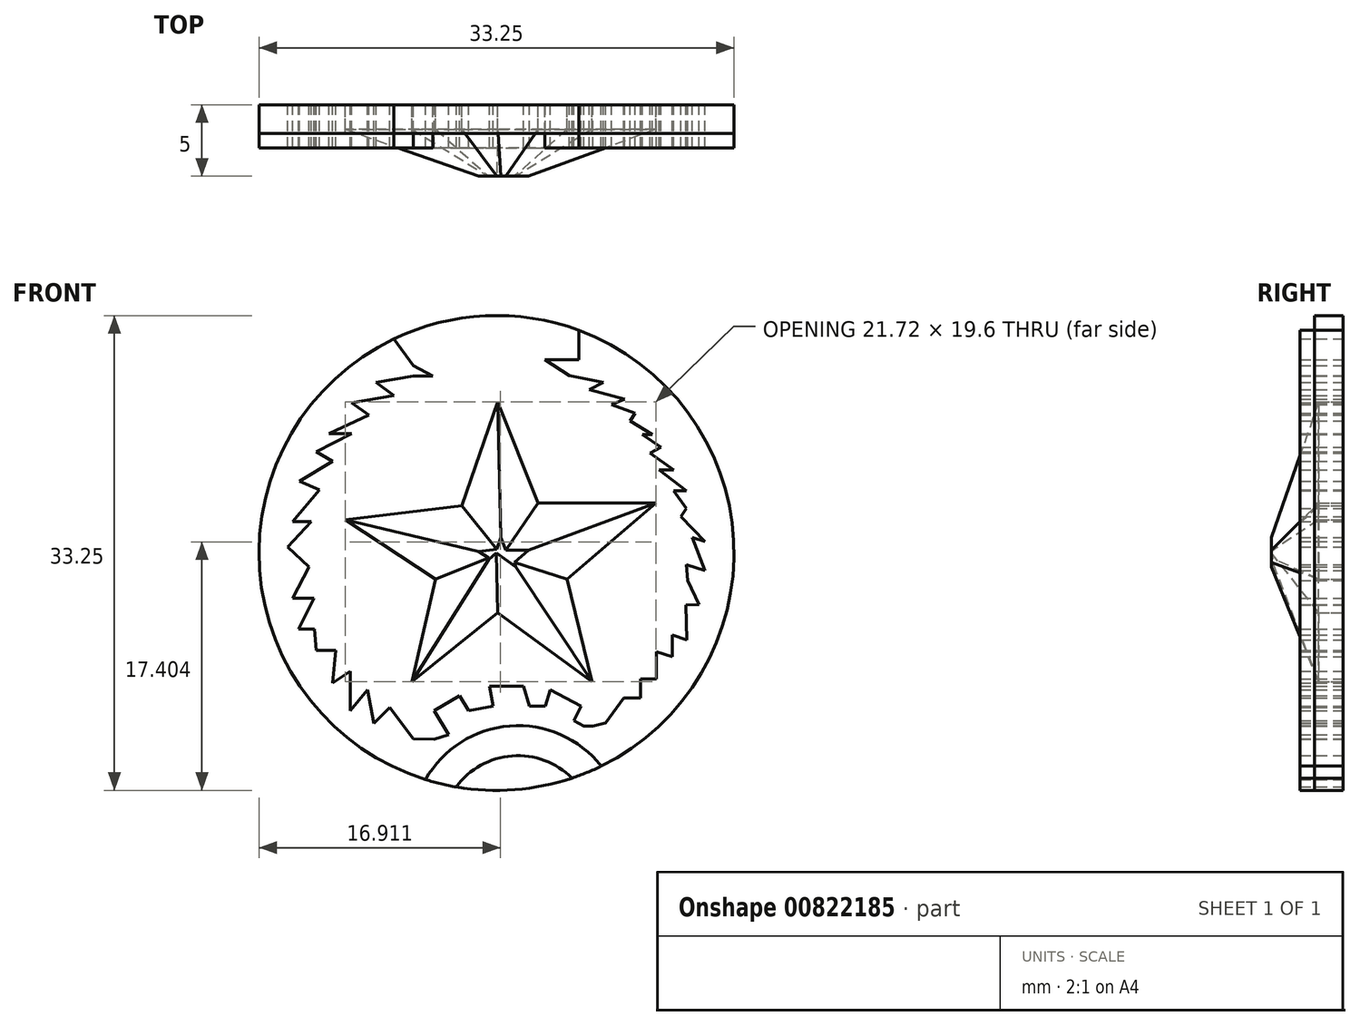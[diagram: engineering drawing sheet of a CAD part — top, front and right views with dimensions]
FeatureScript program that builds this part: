
annotation { "Feature Type Name" : "Feature", "Feature Type Description" : "" }
export const myFeature = defineFeature(function(context is Context, id is Id, definition is map)
    precondition{}
    {
        {
            var Q0;
            Q0=qCreatedBy(makeId("Front.planeOp"),FACE);
            var sketch = newSketch(context, id + "F0", { "sketchPlane" : qUnion([Q0])});
            skLineSegment(sketch, "E0", {"start": v(-2.81, 15.91) * mm, "end": v(-5.33, 8.63) * mm});
            skLineSegment(sketch, "E1", {"start": v(-5.33, 8.63) * mm, "end": v(-13.48, 7.66) * mm});
            skLineSegment(sketch, "E2", {"start": v(-13.48, 7.66) * mm, "end": v(-7.18, 3.5) * mm});
            skLineSegment(sketch, "E3", {"start": v(-7.18, 3.5) * mm, "end": v(-8.83, -3.69) * mm});
            skPoint(sketch, "E4.end.orphan", {"position": v(-2.81, 0) * mm});
            skLineSegment(sketch, "E5", {"start": v(-8.83, -3.69) * mm, "end": v(-2.81, 1.16) * mm});
            skLineSegment(sketch, "E6", {"start": v(-2.81, 1.16) * mm, "end": v(3.78, -3.69) * mm});
            skLineSegment(sketch, "E7", {"start": v(3.78, -3.69) * mm, "end": v(2.04, 3.5) * mm});
            skLineSegment(sketch, "E8", {"start": v(2.04, 3.5) * mm, "end": v(8.24, 8.83) * mm});
            skLineSegment(sketch, "E9", {"start": v(8.24, 8.83) * mm, "end": v(0, 8.83) * mm});
            skLineSegment(sketch, "E10", {"start": v(0, 8.83) * mm, "end": v(-2.81, 15.91) * mm});
            skCircle(sketch, "E11", {"center": v(-2.9, 5.33) * mm, "radius": 16.62 * mm});
            skLineSegment(sketch, "E12", {"start": v(-8.73, -7.66) * mm, "end": v(-7.26, -7.7) * mm});
            skLineSegment(sketch, "E13", {"start": v(-6.25, -7.39) * mm, "end": v(-7.26, -5.72) * mm});
            skLineSegment(sketch, "E14", {"start": v(-7.26, -5.72) * mm, "end": v(-5.5, -4.65) * mm});
            skLineSegment(sketch, "E15", {"start": v(-5.5, -4.65) * mm, "end": v(-4.84, -5.72) * mm});
            skLineSegment(sketch, "E16", {"start": v(-4.84, -5.72) * mm, "end": v(-3.13, -5.4) * mm});
            skLineSegment(sketch, "E17", {"start": v(-3.13, -5.4) * mm, "end": v(-3.4, -4) * mm});
            skLineSegment(sketch, "E18", {"start": v(-3.4, -4) * mm, "end": v(-1.01, -4) * mm});
            skLineSegment(sketch, "E19", {"start": v(-1.01, -4) * mm, "end": v(-0.6, -5.4) * mm});
            skLineSegment(sketch, "E20", {"start": v(-0.6, -5.4) * mm, "end": v(0.5, -5.4) * mm});
            skLineSegment(sketch, "E21", {"start": v(0.5, -5.4) * mm, "end": v(0.86, -4.25) * mm});
            skLineSegment(sketch, "E22", {"start": v(0.86, -4.25) * mm, "end": v(3.02, -5.4) * mm});
            skLineSegment(sketch, "E23", {"start": v(3.02, -5.4) * mm, "end": v(2.5, -6.4) * mm});
            skLineSegment(sketch, "E24", {"start": v(2.5, -6.4) * mm, "end": v(3.21, -6.78) * mm});
            skLineSegment(sketch, "E25", {"start": v(3.21, -6.78) * mm, "end": v(3.84, -6.78) * mm});
            skLineSegment(sketch, "E26", {"start": v(-7.26, -7.7) * mm, "end": v(-6.25, -7.39) * mm});
            skLineSegment(sketch, "E27", {"start": v(4.74, -6.58) * mm, "end": v(6, -4.82) * mm});
            skPoint(sketch, "E27.endSnap0", {"position": v(0.68, -4.82) * mm});
            skLineSegment(sketch, "E28", {"start": v(6, -4.82) * mm, "end": v(7.18, -4.82) * mm});
            skLineSegment(sketch, "E29", {"start": v(7.18, -4.82) * mm, "end": v(7.18, -3.48) * mm});
            skLineSegment(sketch, "E30", {"start": v(7.18, -3.48) * mm, "end": v(8.28, -3.48) * mm});
            skLineSegment(sketch, "E31", {"start": v(8.28, -3.48) * mm, "end": v(8.28, -1.58) * mm});
            skLineSegment(sketch, "E32", {"start": v(8.28, -1.58) * mm, "end": v(9.4, -1.93) * mm});
            skLineSegment(sketch, "E33", {"start": v(9.4, -1.93) * mm, "end": v(9.4, -0.42) * mm});
            skLineSegment(sketch, "E34", {"start": v(9.4, -0.42) * mm, "end": v(10.42, -0.75) * mm});
            skLineSegment(sketch, "E35", {"start": v(10.42, -0.75) * mm, "end": v(10.35, 1.7) * mm});
            skLineSegment(sketch, "E36", {"start": v(10.35, 1.7) * mm, "end": v(11.27, 1.73) * mm});
            skLineSegment(sketch, "E37", {"start": v(11.27, 1.73) * mm, "end": v(10.48, 3.41) * mm});
            skLineSegment(sketch, "E38", {"start": v(10.48, 3.41) * mm, "end": v(10.38, 4.53) * mm});
            skLineSegment(sketch, "E39", {"start": v(10.38, 4.53) * mm, "end": v(11.7, 4.1) * mm});
            skLineSegment(sketch, "E40", {"start": v(11.7, 4.1) * mm, "end": v(10.79, 6.43) * mm});
            skLineSegment(sketch, "E41", {"start": v(10.79, 6.43) * mm, "end": v(11.67, 6.15) * mm});
            skLineSegment(sketch, "E42", {"start": v(11.67, 6.15) * mm, "end": v(10, 7.88) * mm});
            skLineSegment(sketch, "E43", {"start": v(10, 7.88) * mm, "end": v(10.38, 8.47) * mm});
            skLineSegment(sketch, "E44", {"start": v(10.38, 8.47) * mm, "end": v(9.5, 9.68) * mm});
            skLineSegment(sketch, "E45", {"start": v(9.5, 9.68) * mm, "end": v(10.38, 9.68) * mm});
            skLineSegment(sketch, "E46", {"start": v(10.38, 9.68) * mm, "end": v(8.49, 11.16) * mm});
            skLineSegment(sketch, "E47", {"start": v(8.49, 11.16) * mm, "end": v(9.5, 11.16) * mm});
            skLineSegment(sketch, "E48", {"start": v(9.5, 11.16) * mm, "end": v(7.83, 12.34) * mm});
            skLineSegment(sketch, "E49", {"start": v(7.83, 12.34) * mm, "end": v(8.6, 12.75) * mm});
            skLineSegment(sketch, "E50", {"start": v(8.6, 12.75) * mm, "end": v(7.3, 13.63) * mm});
            skLineSegment(sketch, "E51", {"start": v(7.3, 13.63) * mm, "end": v(8, 13.63) * mm});
            skLineSegment(sketch, "E52", {"start": v(8, 13.63) * mm, "end": v(6.44, 14.58) * mm});
            skLineSegment(sketch, "E53", {"start": v(6.44, 14.58) * mm, "end": v(6.8, 15.12) * mm});
            skLineSegment(sketch, "E54", {"start": v(6.8, 15.12) * mm, "end": v(5.16, 15.72) * mm});
            skLineSegment(sketch, "E55", {"start": v(5.16, 15.72) * mm, "end": v(6.07, 16.11) * mm});
            skLineSegment(sketch, "E56", {"start": v(6.07, 16.11) * mm, "end": v(3.6, 16.77) * mm});
            skLineSegment(sketch, "E57", {"start": v(3.6, 16.77) * mm, "end": v(4.57, 17.28) * mm});
            skLineSegment(sketch, "E58", {"start": v(4.57, 17.28) * mm, "end": v(2.19, 17.74) * mm});
            skLineSegment(sketch, "E59", {"start": v(2.19, 17.74) * mm, "end": v(0.48, 18.88) * mm});
            skLineSegment(sketch, "E60", {"start": v(0.48, 18.88) * mm, "end": v(2.85, 18.88) * mm});
            skLineSegment(sketch, "E61", {"start": v(3.84, -6.78) * mm, "end": v(4.74, -6.58) * mm});
            skLineSegment(sketch, "E62", {"start": v(2.85, 18.88) * mm, "end": v(2.85, 20.93) * mm});
            skLineSegment(sketch, "E63", {"start": v(-8.73, -7.66) * mm, "end": v(-10.4, -5.48) * mm});
            skLineSegment(sketch, "E64", {"start": v(-10.4, -5.48) * mm, "end": v(-11.49, -6.58) * mm});
            skLineSegment(sketch, "E65", {"start": v(-11.49, -6.58) * mm, "end": v(-11.93, -4.24) * mm});
            skLineSegment(sketch, "E66", {"start": v(-11.93, -4.24) * mm, "end": v(-13.13, -5.7) * mm});
            skLineSegment(sketch, "E67", {"start": v(-13.13, -5.7) * mm, "end": v(-13.13, -2.94) * mm});
            skLineSegment(sketch, "E68", {"start": v(-13.13, -2.94) * mm, "end": v(-14.37, -3.77) * mm});
            skLineSegment(sketch, "E69", {"start": v(-14.37, -3.77) * mm, "end": v(-14.15, -1.5) * mm});
            skLineSegment(sketch, "E70", {"start": v(-14.15, -1.5) * mm, "end": v(-15.53, -1.5) * mm});
            skLineSegment(sketch, "E71", {"start": v(-15.53, -1.5) * mm, "end": v(-15.66, 0) * mm});
            skLineSegment(sketch, "E72", {"start": v(-15.66, 0) * mm, "end": v(-16.77, 0) * mm});
            skLineSegment(sketch, "E73", {"start": v(-16.77, 0) * mm, "end": v(-15.67, 2.16) * mm});
            skLineSegment(sketch, "E74", {"start": v(-15.67, 2.16) * mm, "end": v(-17.18, 2.16) * mm});
            skLineSegment(sketch, "E75", {"start": v(-17.18, 2.16) * mm, "end": v(-16.03, 4.37) * mm});
            skLineSegment(sketch, "E76", {"start": v(-16.03, 4.37) * mm, "end": v(-17.52, 5.76) * mm});
            skLineSegment(sketch, "E77", {"start": v(-17.52, 5.76) * mm, "end": v(-15.88, 7.53) * mm});
            skLineSegment(sketch, "E78", {"start": v(-15.88, 7.53) * mm, "end": v(-17.18, 7.53) * mm});
            skLineSegment(sketch, "E79", {"start": v(-17.18, 7.53) * mm, "end": v(-15.3, 9.75) * mm});
            skLineSegment(sketch, "E80", {"start": v(-15.3, 9.75) * mm, "end": v(-16.7, 10.35) * mm});
            skLineSegment(sketch, "E81", {"start": v(-16.7, 10.35) * mm, "end": v(-14.38, 11.77) * mm});
            skLineSegment(sketch, "E82", {"start": v(-14.38, 11.77) * mm, "end": v(-15.53, 12.41) * mm});
            skLineSegment(sketch, "E83", {"start": v(-15.53, 12.41) * mm, "end": v(-13.05, 13.7) * mm});
            skLineSegment(sketch, "E84", {"start": v(-13.05, 13.7) * mm, "end": v(-14.64, 13.7) * mm});
            skLineSegment(sketch, "E85", {"start": v(-14.64, 13.7) * mm, "end": v(-11.83, 15) * mm});
            skLineSegment(sketch, "E86", {"start": v(-11.83, 15) * mm, "end": v(-13.07, 15.84) * mm});
            skLineSegment(sketch, "E87", {"start": v(-13.07, 15.84) * mm, "end": v(-10.08, 16.36) * mm});
            skLineSegment(sketch, "E88", {"start": v(-10.08, 16.36) * mm, "end": v(-11.35, 17.28) * mm});
            skLineSegment(sketch, "E89", {"start": v(-11.35, 17.28) * mm, "end": v(-8.73, 17.71) * mm});
            skLineSegment(sketch, "E90", {"start": v(-8.73, 17.71) * mm, "end": v(-7.36, 17.71) * mm});
            skLineSegment(sketch, "E91", {"start": v(-7.36, 17.71) * mm, "end": v(-8.73, 18.45) * mm});
            skLineSegment(sketch, "E92", {"start": v(-8.73, 18.45) * mm, "end": v(-10.08, 20.33) * mm});
            skArc(sketch, "E93", {"start": v(4.43, -9.58) * mm, "mid": v(-1.98, -6.78) * mm, "end": v(-7.88, -10.53) * mm});
            skArc(sketch, "E94.0", {"start": v(2.37, -10.43) * mm, "mid": v(-1.82, -8.87) * mm, "end": v(-5.72, -11.05) * mm});
            skLineSegment(sketch, "E95", {"start": v(-7.18, 3.5) * mm, "end": v(-2.9, 5.33) * mm});
            skLineSegment(sketch, "E96", {"start": v(-13.48, 7.66) * mm, "end": v(-2.9, 5.33) * mm});
            skLineSegment(sketch, "E97", {"start": v(-5.33, 8.63) * mm, "end": v(-2.9, 5.33) * mm});
            skLineSegment(sketch, "E98", {"start": v(0, 8.83) * mm, "end": v(-2.9, 5.33) * mm});
            skLineSegment(sketch, "E99", {"start": v(2.04, 3.5) * mm, "end": v(-2.9, 5.33) * mm});
            skLineSegment(sketch, "E100", {"start": v(8.24, 8.83) * mm, "end": v(-2.9, 5.33) * mm});
            skLineSegment(sketch, "E101", {"start": v(-8.83, -3.69) * mm, "end": v(-2.9, 5.33) * mm});
            skLineSegment(sketch, "E102", {"start": v(-2.81, 1.16) * mm, "end": v(-2.9, 5.33) * mm});
            skLineSegment(sketch, "E103", {"start": v(3.78, -3.69) * mm, "end": v(-2.9, 5.33) * mm});
            skLineSegment(sketch, "E104", {"start": v(-2.81, 15.91) * mm, "end": v(-2.9, 5.33) * mm});
            skSolve(sketch);
        }
        {
            var Q0;
            Q0=makeQuery(id+"F0.imprint","IMPRINT",FACE,{"disambiguationData":[TD([[makeQuery(id+"F0.imprint","IMPRINT",EDGE,{"derivedFrom":sQuery(id+"F0.wireOp",EDGE,"E0")}),1.0]])]});
            var Q1;
            Q1=makeQuery(id+"F0.imprint","IMPRINT",FACE,{"disambiguationData":[TD([[makeQuery(id+"F0.imprint","IMPRINT",EDGE,{"derivedFrom":sQuery(id+"F0.wireOp",EDGE,"E12")}),-1.0]])]});
            var Q2;
            {var subQ0=sQuery(id+"F0.wireOp",EDGE,"E94.0");Q2=makeQuery(id+"F0.imprint","IMPRINT",FACE,{"disambiguationData":[TD([[makeQuery(id+"F0.imprint","IMPRINT",EDGE,{"derivedFrom":subQ0}),1.0]])]});}
            var Q3;
            Q3=makeQuery(id+"F0.imprint","IMPRINT",FACE,{"disambiguationData":[TD([[makeQuery(id+"F0.imprint","IMPRINT",EDGE,{"derivedFrom":sQuery(id+"F0.wireOp",EDGE,"E10")}),1.0]])]});
            var Q4;
            Q4=makeQuery(id+"F0.imprint","IMPRINT",FACE,{"disambiguationData":[TD([[makeQuery(id+"F0.imprint","IMPRINT",EDGE,{"derivedFrom":sQuery(id+"F0.wireOp",EDGE,"E1")}),1.0]])]});
            var Q5;
            Q5=makeQuery(id+"F0.imprint","IMPRINT",FACE,{"disambiguationData":[TD([[makeQuery(id+"F0.imprint","IMPRINT",EDGE,{"derivedFrom":sQuery(id+"F0.wireOp",EDGE,"E2")}),1.0]])]});
            var Q6;
            Q6=makeQuery(id+"F0.imprint","IMPRINT",FACE,{"disambiguationData":[TD([[makeQuery(id+"F0.imprint","IMPRINT",EDGE,{"derivedFrom":sQuery(id+"F0.wireOp",EDGE,"E9")}),1.0]])]});
            var Q7;
            Q7=makeQuery(id+"F0.imprint","IMPRINT",FACE,{"disambiguationData":[TD([[makeQuery(id+"F0.imprint","IMPRINT",EDGE,{"derivedFrom":sQuery(id+"F0.wireOp",EDGE,"E8")}),1.0]])]});
            var Q8;
            Q8=makeQuery(id+"F0.imprint","IMPRINT",FACE,{"disambiguationData":[TD([[makeQuery(id+"F0.imprint","IMPRINT",EDGE,{"derivedFrom":sQuery(id+"F0.wireOp",EDGE,"E3")}),1.0]])]});
            var Q9;
            Q9=makeQuery(id+"F0.imprint","IMPRINT",FACE,{"disambiguationData":[TD([[makeQuery(id+"F0.imprint","IMPRINT",EDGE,{"derivedFrom":sQuery(id+"F0.wireOp",EDGE,"E5")}),1.0]])]});
            var Q10;
            Q10=makeQuery(id+"F0.imprint","IMPRINT",FACE,{"disambiguationData":[TD([[makeQuery(id+"F0.imprint","IMPRINT",EDGE,{"derivedFrom":sQuery(id+"F0.wireOp",EDGE,"E6")}),1.0]])]});
            var Q11;
            Q11=makeQuery(id+"F0.imprint","IMPRINT",FACE,{"disambiguationData":[TD([[makeQuery(id+"F0.imprint","IMPRINT",EDGE,{"derivedFrom":sQuery(id+"F0.wireOp",EDGE,"E7")}),1.0]])]});
            extrude(context, id + "F1", {"entities" : qUnion([Q0, Q1, Q2, Q3, Q4, Q5, Q6, Q7, Q8, Q9, Q10, Q11]), "depth" : 3 * mm, "offsetDistance" : 25 * mm});
        }
        {
            var Q0;
            Q0 = qSketchRegion(id + "F0", true);
            extrude(context, id + "F2", {"entities" : qUnion([Q0]), "depth" : 2 * mm, "offsetDistance" : 25 * mm});
        }
        {
            var Q0;
            Q0=makeQuery(id+"F1.opExtrude","CAP_FACE",FACE,{"disambiguationData":[OSD([sQuery(id+"F0.wireOp",EDGE,"E0"),sQuery(id+"F0.wireOp",EDGE,"E1"),sQuery(id+"F0.wireOp",EDGE,"E2"),sQuery(id+"F0.wireOp",EDGE,"E3"),sQuery(id+"F0.wireOp",EDGE,"E5"),sQuery(id+"F0.wireOp",EDGE,"E6"),sQuery(id+"F0.wireOp",EDGE,"E7"),sQuery(id+"F0.wireOp",EDGE,"E8"),sQuery(id+"F0.wireOp",EDGE,"E9"),sQuery(id+"F0.wireOp",EDGE,"E10")])],"isStart":false});
            extrude(context, id + "F3", {"entities" : qUnion([Q0]), "operationType" : NewBodyOperationType.ADD, "depth" : 2 * mm, "offsetDistance" : 25 * mm});
        }
        {
            var Q0;
            Q0=makeQuery(id+"F3.opExtrude","CAP_FACE",FACE,{"disambiguationData":[OSD([sQuery(id+"F0.wireOp",EDGE,"E0"),sQuery(id+"F0.wireOp",EDGE,"E1"),sQuery(id+"F0.wireOp",EDGE,"E2"),sQuery(id+"F0.wireOp",EDGE,"E3"),sQuery(id+"F0.wireOp",EDGE,"E5"),sQuery(id+"F0.wireOp",EDGE,"E6"),sQuery(id+"F0.wireOp",EDGE,"E7"),sQuery(id+"F0.wireOp",EDGE,"E8"),sQuery(id+"F0.wireOp",EDGE,"E9"),sQuery(id+"F0.wireOp",EDGE,"E10")])],"isStart":false});
            chamfer(context, id + "F4", {"entities" : qUnion([Q0]), "width" : 3.3 * mm, "tangentPropagation" : true});
        }
        {
            var Q0;
            Q0=makeQuery(id+"F1.opExtrude","CAP_FACE",FACE,{"disambiguationData":[OSD([sQuery(id+"F0.wireOp",EDGE,"E11"),sQuery(id+"F0.wireOp",EDGE,"E12"),sQuery(id+"F0.wireOp",EDGE,"E13"),sQuery(id+"F0.wireOp",EDGE,"E14"),sQuery(id+"F0.wireOp",EDGE,"E15"),sQuery(id+"F0.wireOp",EDGE,"E16"),sQuery(id+"F0.wireOp",EDGE,"E17"),sQuery(id+"F0.wireOp",EDGE,"E18"),sQuery(id+"F0.wireOp",EDGE,"E19"),sQuery(id+"F0.wireOp",EDGE,"E20"),sQuery(id+"F0.wireOp",EDGE,"E21"),sQuery(id+"F0.wireOp",EDGE,"E22"),sQuery(id+"F0.wireOp",EDGE,"E23"),sQuery(id+"F0.wireOp",EDGE,"E24"),sQuery(id+"F0.wireOp",EDGE,"E25"),sQuery(id+"F0.wireOp",EDGE,"E26"),sQuery(id+"F0.wireOp",EDGE,"E27"),sQuery(id+"F0.wireOp",EDGE,"E28"),sQuery(id+"F0.wireOp",EDGE,"E29"),sQuery(id+"F0.wireOp",EDGE,"E30"),sQuery(id+"F0.wireOp",EDGE,"E31"),sQuery(id+"F0.wireOp",EDGE,"E32"),sQuery(id+"F0.wireOp",EDGE,"E33"),sQuery(id+"F0.wireOp",EDGE,"E34"),sQuery(id+"F0.wireOp",EDGE,"E35"),sQuery(id+"F0.wireOp",EDGE,"E36"),sQuery(id+"F0.wireOp",EDGE,"E37"),sQuery(id+"F0.wireOp",EDGE,"E38"),sQuery(id+"F0.wireOp",EDGE,"E39"),sQuery(id+"F0.wireOp",EDGE,"E40"),sQuery(id+"F0.wireOp",EDGE,"E41"),sQuery(id+"F0.wireOp",EDGE,"E42"),sQuery(id+"F0.wireOp",EDGE,"E43"),sQuery(id+"F0.wireOp",EDGE,"E44"),sQuery(id+"F0.wireOp",EDGE,"E45"),sQuery(id+"F0.wireOp",EDGE,"E46"),sQuery(id+"F0.wireOp",EDGE,"E47"),sQuery(id+"F0.wireOp",EDGE,"E48"),sQuery(id+"F0.wireOp",EDGE,"E49"),sQuery(id+"F0.wireOp",EDGE,"E50"),sQuery(id+"F0.wireOp",EDGE,"E51"),sQuery(id+"F0.wireOp",EDGE,"E52"),sQuery(id+"F0.wireOp",EDGE,"E53"),sQuery(id+"F0.wireOp",EDGE,"E54"),sQuery(id+"F0.wireOp",EDGE,"E55"),sQuery(id+"F0.wireOp",EDGE,"E56"),sQuery(id+"F0.wireOp",EDGE,"E57"),sQuery(id+"F0.wireOp",EDGE,"E58"),sQuery(id+"F0.wireOp",EDGE,"E59"),sQuery(id+"F0.wireOp",EDGE,"E60"),sQuery(id+"F0.wireOp",EDGE,"E61"),sQuery(id+"F0.wireOp",EDGE,"E62"),sQuery(id+"F0.wireOp",EDGE,"E63"),sQuery(id+"F0.wireOp",EDGE,"E64"),sQuery(id+"F0.wireOp",EDGE,"E65"),sQuery(id+"F0.wireOp",EDGE,"E66"),sQuery(id+"F0.wireOp",EDGE,"E67"),sQuery(id+"F0.wireOp",EDGE,"E68"),sQuery(id+"F0.wireOp",EDGE,"E69"),sQuery(id+"F0.wireOp",EDGE,"E70"),sQuery(id+"F0.wireOp",EDGE,"E71"),sQuery(id+"F0.wireOp",EDGE,"E72"),sQuery(id+"F0.wireOp",EDGE,"E73"),sQuery(id+"F0.wireOp",EDGE,"E74"),sQuery(id+"F0.wireOp",EDGE,"E75"),sQuery(id+"F0.wireOp",EDGE,"E76"),sQuery(id+"F0.wireOp",EDGE,"E77"),sQuery(id+"F0.wireOp",EDGE,"E78"),sQuery(id+"F0.wireOp",EDGE,"E79"),sQuery(id+"F0.wireOp",EDGE,"E80"),sQuery(id+"F0.wireOp",EDGE,"E81"),sQuery(id+"F0.wireOp",EDGE,"E82"),sQuery(id+"F0.wireOp",EDGE,"E83"),sQuery(id+"F0.wireOp",EDGE,"E84"),sQuery(id+"F0.wireOp",EDGE,"E85"),sQuery(id+"F0.wireOp",EDGE,"E86"),sQuery(id+"F0.wireOp",EDGE,"E87"),sQuery(id+"F0.wireOp",EDGE,"E88"),sQuery(id+"F0.wireOp",EDGE,"E89"),sQuery(id+"F0.wireOp",EDGE,"E90"),sQuery(id+"F0.wireOp",EDGE,"E91"),sQuery(id+"F0.wireOp",EDGE,"E92"),sQuery(id+"F0.wireOp",EDGE,"E93")])],"isStart":false});
            extrude(context, id + "F5", {"entities" : qUnion([Q0]), "operationType" : NewBodyOperationType.ADD, "depth" : 2 * mm, "offsetDistance" : 25 * mm});
        }
        {
            var Q0;
            Q0=makeQuery(id+"F1.opExtrude","CAP_FACE",FACE,{"disambiguationData":[OSD([sQuery(id+"F0.wireOp",EDGE,"E11"),sQuery(id+"F0.wireOp",EDGE,"E94.0")])],"isStart":false});
            extrude(context, id + "F6", {"entities" : qUnion([Q0]), "operationType" : NewBodyOperationType.ADD, "depth" : 2 * mm, "offsetDistance" : 25 * mm});
        }
        {
            var Q0;
            Q0=makeQuery(id+"F5.opExtrude","CAP_FACE",FACE,{"disambiguationData":[OSD([sQuery(id+"F0.wireOp",EDGE,"E11"),sQuery(id+"F0.wireOp",EDGE,"E12"),sQuery(id+"F0.wireOp",EDGE,"E13"),sQuery(id+"F0.wireOp",EDGE,"E14"),sQuery(id+"F0.wireOp",EDGE,"E15"),sQuery(id+"F0.wireOp",EDGE,"E16"),sQuery(id+"F0.wireOp",EDGE,"E17"),sQuery(id+"F0.wireOp",EDGE,"E18"),sQuery(id+"F0.wireOp",EDGE,"E19"),sQuery(id+"F0.wireOp",EDGE,"E20"),sQuery(id+"F0.wireOp",EDGE,"E21"),sQuery(id+"F0.wireOp",EDGE,"E22"),sQuery(id+"F0.wireOp",EDGE,"E23"),sQuery(id+"F0.wireOp",EDGE,"E24"),sQuery(id+"F0.wireOp",EDGE,"E25"),sQuery(id+"F0.wireOp",EDGE,"E26"),sQuery(id+"F0.wireOp",EDGE,"E27"),sQuery(id+"F0.wireOp",EDGE,"E28"),sQuery(id+"F0.wireOp",EDGE,"E29"),sQuery(id+"F0.wireOp",EDGE,"E30"),sQuery(id+"F0.wireOp",EDGE,"E31"),sQuery(id+"F0.wireOp",EDGE,"E32"),sQuery(id+"F0.wireOp",EDGE,"E33"),sQuery(id+"F0.wireOp",EDGE,"E34"),sQuery(id+"F0.wireOp",EDGE,"E35"),sQuery(id+"F0.wireOp",EDGE,"E36"),sQuery(id+"F0.wireOp",EDGE,"E37"),sQuery(id+"F0.wireOp",EDGE,"E38"),sQuery(id+"F0.wireOp",EDGE,"E39"),sQuery(id+"F0.wireOp",EDGE,"E40"),sQuery(id+"F0.wireOp",EDGE,"E41"),sQuery(id+"F0.wireOp",EDGE,"E42"),sQuery(id+"F0.wireOp",EDGE,"E43"),sQuery(id+"F0.wireOp",EDGE,"E44"),sQuery(id+"F0.wireOp",EDGE,"E45"),sQuery(id+"F0.wireOp",EDGE,"E46"),sQuery(id+"F0.wireOp",EDGE,"E47"),sQuery(id+"F0.wireOp",EDGE,"E48"),sQuery(id+"F0.wireOp",EDGE,"E49"),sQuery(id+"F0.wireOp",EDGE,"E50"),sQuery(id+"F0.wireOp",EDGE,"E51"),sQuery(id+"F0.wireOp",EDGE,"E52"),sQuery(id+"F0.wireOp",EDGE,"E53"),sQuery(id+"F0.wireOp",EDGE,"E54"),sQuery(id+"F0.wireOp",EDGE,"E55"),sQuery(id+"F0.wireOp",EDGE,"E56"),sQuery(id+"F0.wireOp",EDGE,"E57"),sQuery(id+"F0.wireOp",EDGE,"E58"),sQuery(id+"F0.wireOp",EDGE,"E59"),sQuery(id+"F0.wireOp",EDGE,"E60"),sQuery(id+"F0.wireOp",EDGE,"E61"),sQuery(id+"F0.wireOp",EDGE,"E62"),sQuery(id+"F0.wireOp",EDGE,"E63"),sQuery(id+"F0.wireOp",EDGE,"E64"),sQuery(id+"F0.wireOp",EDGE,"E65"),sQuery(id+"F0.wireOp",EDGE,"E66"),sQuery(id+"F0.wireOp",EDGE,"E67"),sQuery(id+"F0.wireOp",EDGE,"E68"),sQuery(id+"F0.wireOp",EDGE,"E69"),sQuery(id+"F0.wireOp",EDGE,"E70"),sQuery(id+"F0.wireOp",EDGE,"E71"),sQuery(id+"F0.wireOp",EDGE,"E72"),sQuery(id+"F0.wireOp",EDGE,"E73"),sQuery(id+"F0.wireOp",EDGE,"E74"),sQuery(id+"F0.wireOp",EDGE,"E75"),sQuery(id+"F0.wireOp",EDGE,"E76"),sQuery(id+"F0.wireOp",EDGE,"E77"),sQuery(id+"F0.wireOp",EDGE,"E78"),sQuery(id+"F0.wireOp",EDGE,"E79"),sQuery(id+"F0.wireOp",EDGE,"E80"),sQuery(id+"F0.wireOp",EDGE,"E81"),sQuery(id+"F0.wireOp",EDGE,"E82"),sQuery(id+"F0.wireOp",EDGE,"E83"),sQuery(id+"F0.wireOp",EDGE,"E84"),sQuery(id+"F0.wireOp",EDGE,"E85"),sQuery(id+"F0.wireOp",EDGE,"E86"),sQuery(id+"F0.wireOp",EDGE,"E87"),sQuery(id+"F0.wireOp",EDGE,"E88"),sQuery(id+"F0.wireOp",EDGE,"E89"),sQuery(id+"F0.wireOp",EDGE,"E90"),sQuery(id+"F0.wireOp",EDGE,"E91"),sQuery(id+"F0.wireOp",EDGE,"E92"),sQuery(id+"F0.wireOp",EDGE,"E93")])],"isStart":false});
            extrude(context, id + "F7", {"entities" : qUnion([Q0]), "operationType" : NewBodyOperationType.REMOVE, "depth" : 2 * mm, "offsetDistance" : 25 * mm});
        }
        {
            var Q0;
            Q0=makeQuery(id+"F5.opExtrude","CAP_FACE",FACE,{"disambiguationData":[OSD([sQuery(id+"F0.wireOp",EDGE,"E11"),sQuery(id+"F0.wireOp",EDGE,"E12"),sQuery(id+"F0.wireOp",EDGE,"E13"),sQuery(id+"F0.wireOp",EDGE,"E14"),sQuery(id+"F0.wireOp",EDGE,"E15"),sQuery(id+"F0.wireOp",EDGE,"E16"),sQuery(id+"F0.wireOp",EDGE,"E17"),sQuery(id+"F0.wireOp",EDGE,"E18"),sQuery(id+"F0.wireOp",EDGE,"E19"),sQuery(id+"F0.wireOp",EDGE,"E20"),sQuery(id+"F0.wireOp",EDGE,"E21"),sQuery(id+"F0.wireOp",EDGE,"E22"),sQuery(id+"F0.wireOp",EDGE,"E23"),sQuery(id+"F0.wireOp",EDGE,"E24"),sQuery(id+"F0.wireOp",EDGE,"E25"),sQuery(id+"F0.wireOp",EDGE,"E26"),sQuery(id+"F0.wireOp",EDGE,"E27"),sQuery(id+"F0.wireOp",EDGE,"E28"),sQuery(id+"F0.wireOp",EDGE,"E29"),sQuery(id+"F0.wireOp",EDGE,"E30"),sQuery(id+"F0.wireOp",EDGE,"E31"),sQuery(id+"F0.wireOp",EDGE,"E32"),sQuery(id+"F0.wireOp",EDGE,"E33"),sQuery(id+"F0.wireOp",EDGE,"E34"),sQuery(id+"F0.wireOp",EDGE,"E35"),sQuery(id+"F0.wireOp",EDGE,"E36"),sQuery(id+"F0.wireOp",EDGE,"E37"),sQuery(id+"F0.wireOp",EDGE,"E38"),sQuery(id+"F0.wireOp",EDGE,"E39"),sQuery(id+"F0.wireOp",EDGE,"E40"),sQuery(id+"F0.wireOp",EDGE,"E41"),sQuery(id+"F0.wireOp",EDGE,"E42"),sQuery(id+"F0.wireOp",EDGE,"E43"),sQuery(id+"F0.wireOp",EDGE,"E44"),sQuery(id+"F0.wireOp",EDGE,"E45"),sQuery(id+"F0.wireOp",EDGE,"E46"),sQuery(id+"F0.wireOp",EDGE,"E47"),sQuery(id+"F0.wireOp",EDGE,"E48"),sQuery(id+"F0.wireOp",EDGE,"E49"),sQuery(id+"F0.wireOp",EDGE,"E50"),sQuery(id+"F0.wireOp",EDGE,"E51"),sQuery(id+"F0.wireOp",EDGE,"E52"),sQuery(id+"F0.wireOp",EDGE,"E53"),sQuery(id+"F0.wireOp",EDGE,"E54"),sQuery(id+"F0.wireOp",EDGE,"E55"),sQuery(id+"F0.wireOp",EDGE,"E56"),sQuery(id+"F0.wireOp",EDGE,"E57"),sQuery(id+"F0.wireOp",EDGE,"E58"),sQuery(id+"F0.wireOp",EDGE,"E59"),sQuery(id+"F0.wireOp",EDGE,"E60"),sQuery(id+"F0.wireOp",EDGE,"E61"),sQuery(id+"F0.wireOp",EDGE,"E62"),sQuery(id+"F0.wireOp",EDGE,"E63"),sQuery(id+"F0.wireOp",EDGE,"E64"),sQuery(id+"F0.wireOp",EDGE,"E65"),sQuery(id+"F0.wireOp",EDGE,"E66"),sQuery(id+"F0.wireOp",EDGE,"E67"),sQuery(id+"F0.wireOp",EDGE,"E68"),sQuery(id+"F0.wireOp",EDGE,"E69"),sQuery(id+"F0.wireOp",EDGE,"E70"),sQuery(id+"F0.wireOp",EDGE,"E71"),sQuery(id+"F0.wireOp",EDGE,"E72"),sQuery(id+"F0.wireOp",EDGE,"E73"),sQuery(id+"F0.wireOp",EDGE,"E74"),sQuery(id+"F0.wireOp",EDGE,"E75"),sQuery(id+"F0.wireOp",EDGE,"E76"),sQuery(id+"F0.wireOp",EDGE,"E77"),sQuery(id+"F0.wireOp",EDGE,"E78"),sQuery(id+"F0.wireOp",EDGE,"E79"),sQuery(id+"F0.wireOp",EDGE,"E80"),sQuery(id+"F0.wireOp",EDGE,"E81"),sQuery(id+"F0.wireOp",EDGE,"E82"),sQuery(id+"F0.wireOp",EDGE,"E83"),sQuery(id+"F0.wireOp",EDGE,"E84"),sQuery(id+"F0.wireOp",EDGE,"E85"),sQuery(id+"F0.wireOp",EDGE,"E86"),sQuery(id+"F0.wireOp",EDGE,"E87"),sQuery(id+"F0.wireOp",EDGE,"E88"),sQuery(id+"F0.wireOp",EDGE,"E89"),sQuery(id+"F0.wireOp",EDGE,"E90"),sQuery(id+"F0.wireOp",EDGE,"E91"),sQuery(id+"F0.wireOp",EDGE,"E92"),sQuery(id+"F0.wireOp",EDGE,"E93")])],"isStart":false});
            extrude(context, id + "F8", {"entities" : qUnion([Q0]), "operationType" : NewBodyOperationType.REMOVE, "oppositeDirection" : true, "depth" : 2 * mm, "offsetDistance" : 25 * mm});
        }
        {
            var Q0;
            Q0=makeQuery(id+"F6.opExtrude","CAP_FACE",FACE,{"disambiguationData":[OSD([sQuery(id+"F0.wireOp",EDGE,"E11"),sQuery(id+"F0.wireOp",EDGE,"E94.0")])],"isStart":false});
            extrude(context, id + "F9", {"entities" : qUnion([Q0]), "operationType" : NewBodyOperationType.REMOVE, "oppositeDirection" : true, "depth" : 2 * mm, "offsetDistance" : 25 * mm});
        }
    });
